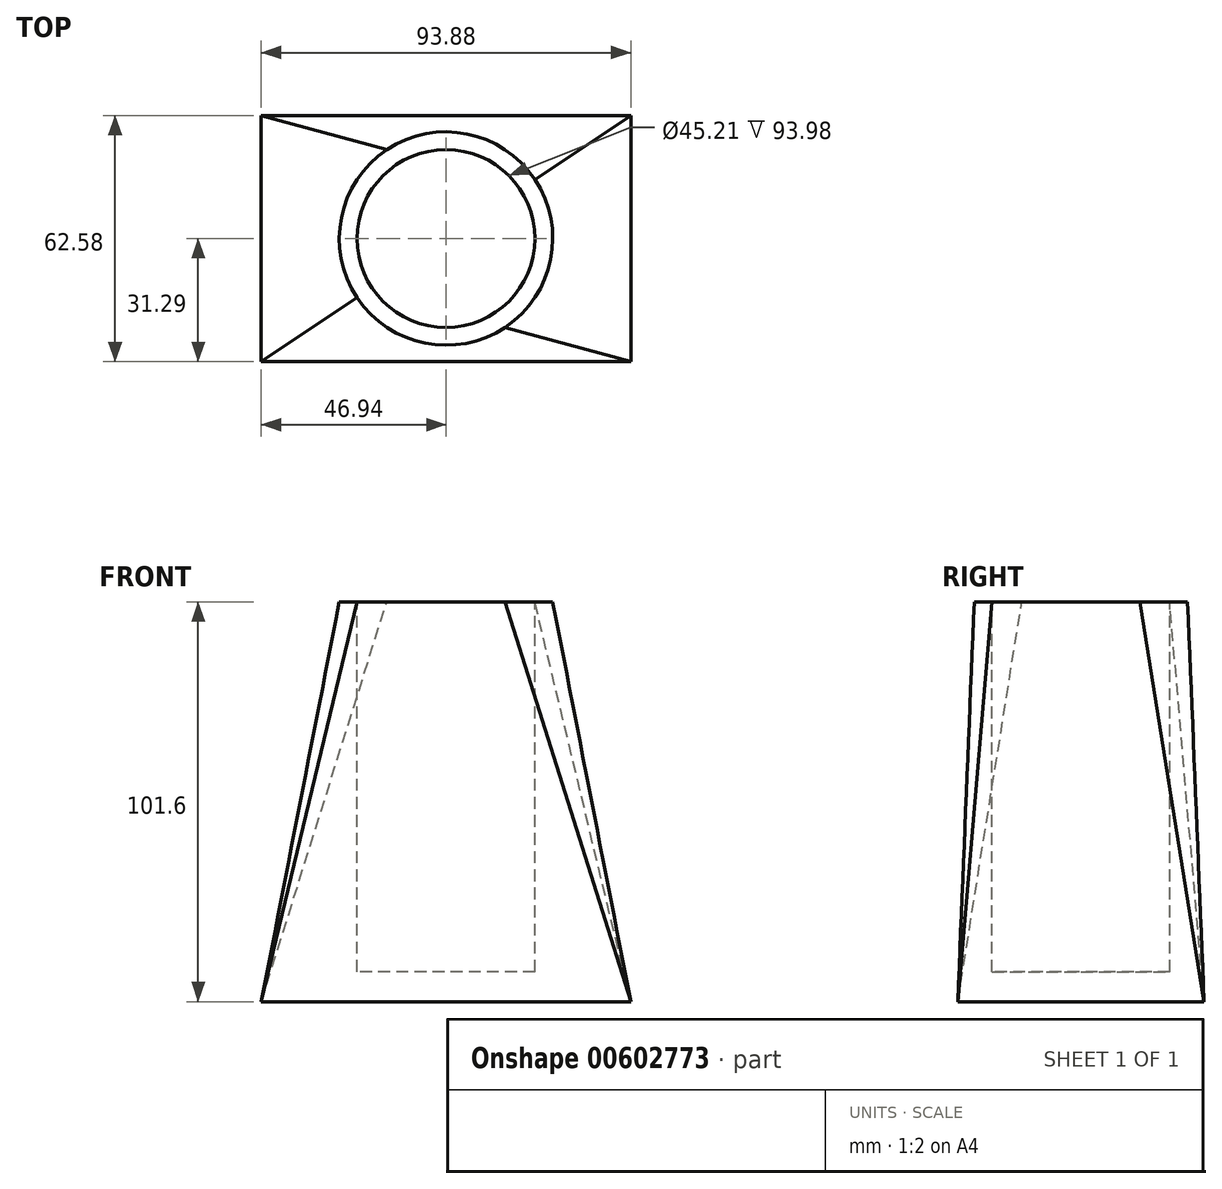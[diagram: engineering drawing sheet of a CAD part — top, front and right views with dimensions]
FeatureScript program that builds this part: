
annotation { "Feature Type Name" : "Feature", "Feature Type Description" : "" }
export const myFeature = defineFeature(function(context is Context, id is Id, definition is map)
    precondition{}
    {
        {
            var Q0;
            Q0=qCreatedBy(makeId("Top.planeOp"),FACE);
            var sketch = newSketch(context, id + "F0", { "sketchPlane" : qUnion([Q0])});
            skLineSegment(sketch, "E0.bottom", {"start": v(38.1, -28.89) * mm, "end": v(-38.1, -28.89) * mm});
            skLineSegment(sketch, "E0.top", {"start": v(38.1, 28.89) * mm, "end": v(-38.1, 28.89) * mm});
            skLineSegment(sketch, "E0.left", {"start": v(38.1, -28.89) * mm, "end": v(38.1, 28.89) * mm});
            skLineSegment(sketch, "E0.right", {"start": v(-38.1, -28.89) * mm, "end": v(-38.1, 28.89) * mm});
            skPoint(sketch, "E0.middle", {"position": v(0, 0) * mm});
            skLineSegment(sketch, "E1.bottom", {"start": v(31.75, 22.54) * mm, "end": v(-31.75, 22.54) * mm});
            skLineSegment(sketch, "E1.top", {"start": v(31.75, -22.54) * mm, "end": v(-31.75, -22.54) * mm});
            skLineSegment(sketch, "E1.left", {"start": v(31.75, 22.54) * mm, "end": v(31.75, -22.54) * mm});
            skLineSegment(sketch, "E1.right", {"start": v(-31.75, 22.54) * mm, "end": v(-31.75, -22.54) * mm});
            skSolve(sketch);
        }
        {
            var Q0;
            Q0=qCreatedBy(makeId("Top.planeOp"),FACE);
            cPlane(context, id + "F1", {"entities" : qUnion([Q0]), "cplaneType" : CPlaneType.OFFSET, "offset" : 101.6 * mm, "width" : 152.4 * mm, "height" : 152.4 * mm});
        }
        {
            var Q0;
            Q0=qCreatedBy(id+"F1.planeOp",FACE);
            var sketch = newSketch(context, id + "F2", { "sketchPlane" : qUnion([Q0])});
            skCircle(sketch, "E2", {"center": v(0, 0) * mm, "radius": 28.46 * mm});
            skCircle(sketch, "E3", {"center": v(0, 0) * mm, "radius": 22.69 * mm});
            skSolve(sketch);
        }
        {
            var Q0;
            Q0=makeQuery(id+"F0.imprint","IMPRINT",FACE,{"disambiguationData":[TD([[makeQuery(id+"F0.imprint","IMPRINT",EDGE,{"derivedFrom":sQuery(id+"F0.wireOp",EDGE,"E1.bottom")}),1.0]])]});
            var Q1;
            Q1=makeQuery(id+"F2.imprint","IMPRINT",FACE,{"disambiguationData":[TD([[makeQuery(id+"F2.imprint","IMPRINT",EDGE,{"derivedFrom":sQuery(id+"F2.wireOp",EDGE,"E3")}),1.0]])]});
            var Q2;
            Q2=makeQuery(id+"F0.imprint","IMPRINT",FACE,{"disambiguationData":[TD([[makeQuery(id+"F0.imprint","IMPRINT",EDGE,{"derivedFrom":sQuery(id+"F0.wireOp",EDGE,"E1.bottom")}),1.0]])]});
            var Q3;
            Q3=sQuery(id+"F2.wireOp",EDGE,"E3");
            loft(context, id + "F3", {"bodyType" : ToolBodyType.SURFACE, "sheetProfilesArray" : [{ "sheetProfileEntities" : qUnion([Q0]) }, { "sheetProfileEntities" : qUnion([Q1]) }], "wireProfilesArray" : [{ "wireProfileEntities" : qUnion([Q2]) }, { "wireProfileEntities" : qUnion([Q3]) }]});
        }
        {
            var Q0;
            Q0=qCreatedBy(id+"F1.planeOp",FACE);
            var sketch = newSketch(context, id + "F4", { "sketchPlane" : qUnion([Q0])});
            skCircle(sketch, "E4", {"center": v(0, 0) * mm, "radius": 27.1 * mm});
            skSolve(sketch);
        }
        {
            var Q0;
            Q0=qCreatedBy(makeId("Top.planeOp"),FACE);
            var sketch = newSketch(context, id + "F5", { "sketchPlane" : qUnion([Q0])});
            skLineSegment(sketch, "E5.bottom", {"start": v(46.94, 31.3) * mm, "end": v(-46.94, 31.3) * mm});
            skLineSegment(sketch, "E5.top", {"start": v(46.94, -31.3) * mm, "end": v(-46.94, -31.3) * mm});
            skLineSegment(sketch, "E5.left", {"start": v(46.94, 31.3) * mm, "end": v(46.94, -31.3) * mm});
            skLineSegment(sketch, "E5.right", {"start": v(-46.94, 31.3) * mm, "end": v(-46.94, -31.3) * mm});
            skPoint(sketch, "E5.middle", {"position": v(0, 0) * mm});
            skSolve(sketch);
        }
        {
            var Q0;
            Q0=makeQuery(id+"F5.imprint","IMPRINT",FACE,{"disambiguationData":[TD([[makeQuery(id+"F5.imprint","IMPRINT",EDGE,{"derivedFrom":sQuery(id+"F5.wireOp",EDGE,"E5.bottom")}),1.0]])]});
            var Q1;
            Q1=makeQuery(id+"F4.imprint","IMPRINT",FACE,{"disambiguationData":[TD([[makeQuery(id+"F4.imprint","IMPRINT",EDGE,{"derivedFrom":sQuery(id+"F4.wireOp",EDGE,"E4")}),1.0]])]});
            loft(context, id + "F6", {"sheetProfilesArray" : [{ "sheetProfileEntities" : qUnion([Q0]) }, { "sheetProfileEntities" : qUnion([Q1]) }]});
        }
        {
            var Q0;
            Q0=qCreatedBy(id+"F1.planeOp",FACE);
            var sketch = newSketch(context, id + "F7", { "sketchPlane" : qUnion([Q0])});
            skCircle(sketch, "E6", {"center": v(0, 0) * mm, "radius": 22.6 * mm});
            skSolve(sketch);
        }
        {
            var Q0;
            Q0 = qSketchRegion(id + "F7", true);
            extrude(context, id + "F8", {"entities" : qUnion([Q0]), "operationType" : NewBodyOperationType.REMOVE, "oppositeDirection" : true, "depth" : 93.98 * mm, "offsetDistance" : 25.4 * mm});
        }
    });
